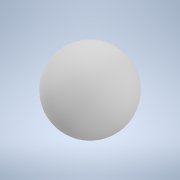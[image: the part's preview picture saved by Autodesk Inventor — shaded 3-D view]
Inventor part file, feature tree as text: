
AUTODESK INVENTOR PART (.ipt)
format: ipt  version: 2021 (Build 250183000, 183)  size: 113,664 bytes
history: native  units: mm
features: revolve x1, sketch x1
ambient origin geometry x8: Origin, YZ Plane, XZ Plane, XY Plane, X Axis, Y Axis, Z Axis, Center Point
bodies: Solid1 (feature_tree)
feature tree (2):
  revolve  "Revolution1"  [1 undecoded]
  sketch  "Sketch1"  dims[d0=90.0deg]
note: 1 required parameter value undecoded (feature->parameter linkage not recoverable at this tier; creation-order binding heuristic only, values carry confidence <= 0.55)
